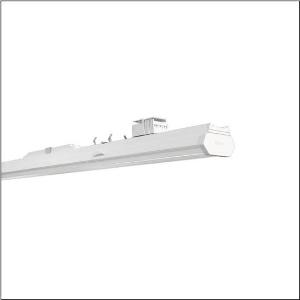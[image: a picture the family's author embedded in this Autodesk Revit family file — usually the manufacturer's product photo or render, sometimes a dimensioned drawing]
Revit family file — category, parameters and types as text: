
# Revit family: licross_11_protected_ho_51tp12dn4fxm3s4
name_source: partatom
category: Lighting Fixtures
units: mm (PartAtom-declared; Revit-internal decimal feet)

## family parameters
Cut with Voids When Loaded = No
Host = Face
Light Source = No
Part Type = Normal
Room Calculation Point = No
Round Connector Dimension = Use Diameter
Shared = No

## types (1)
- --- (1 x LED, 970 lm, 7.4 W, 4000K)
    Apparent Load = 7 VA
    CIE Flux Codes = 70 91 97 98 100
    Color Rendering = 80
    Color Temperature = 4000K
    Default Elevation = 1800 mm
    Description = Licross 11 Protected HO, luminaire insert, of sheet steel, galvanised, coil coated, white, length: 1.500mm, width: 90mm, height: 101mm, LED rated luminous flux: 15.270lm, light colour: 840, SDCM (Standard Deviation of Colour Matching)MacAdam ≤ 2 SDCM (initial), control gear: DALI 2, with plug, 6-pole, with phase selection, for trunking rail, 9 or 11-core, mains connection: 220..240V, AC, 50/60Hz, rated input power: 91W, for trunking rail, 9-/11-core, internal wiring halogen-free, for emergency light function, converter,control gear: single battery element, battery: LiFePO4, 9Ah, primary light control with lens, of plastic, primary optical cover: cover, of PMMA, light emission: direct distribution, primary light characteristic: symmetric, protection rating (complete): IP64, insulation class (complete): insulation class I (protective earthing), certification: CE, UKCA, protection symbol: D if used in an environment with conductive dust loads with corresponding accessories, impact resistance: IK06, permissible ambient temperature for indoor applications: +5..+30°C, standard: EN 60598-2-22, LABS conformity tested according to VDMA 24364:2018-05, reducing of maximum allowable ambient temperature of 5°C with ceiling mounting, corresponds to IFS (International Featured Standards) requirements for safety and quality in the food industry, The light source and the operating device comply with the requirements of the Ecodesign Regulation (EU) 2019/2020 and are replaceable in accordance with this regulation, packaging unit: 1 piece
    Height = 92 mm
    Lamp = 1 x LED
    Lamp Light Flux = 970 lm
    Lamp Power = 7.4 W
    Lamp count = 1
    Length = 1500 mm
    Luminous efficacy = 131 lm/W
    Manufacturer = Siteco
    ModVariant = No
    Model = 51TP12DN4FXM3S4
    Mounting Place = Ceiling
    Mounting Type = Pendant
    Number of Poles = 1
    OnlyDefault = Yes
    Power Factor = 1
    Product Name = Licross 11 Protected HO
    Product group = luminaire insert | ceiling pendant
    ProductGroupID = 901
    Protection Class = Protection class I
    Protection Degree = IP 64
    RLX_Detail_Level = 1
    RLX_Emergency_Light_Flux = 0 lm
    RLX_Emergency_Type = 0
    RLX_Emergency_Type_DB = No
    RlxData = <blob elided: 25105 chars, md5=53e291d8>
    Socket = socket
    Standby Power = 0 W
    System Light Flux = 970 lm
    System Power = 7 W
    Type Comments = : emergency light operation: 3 h
    Type Image = l_1256148.jpg
    URL = http://relux.com
    VarID = @adj_096255
    Voltage = 0 V
    Weight = 0.00 kg
    Width = 88 mm

## geometry (parser evidence)
native form markers: Blend x4, Sweep x9
no freeform markers — native parametric forms only
